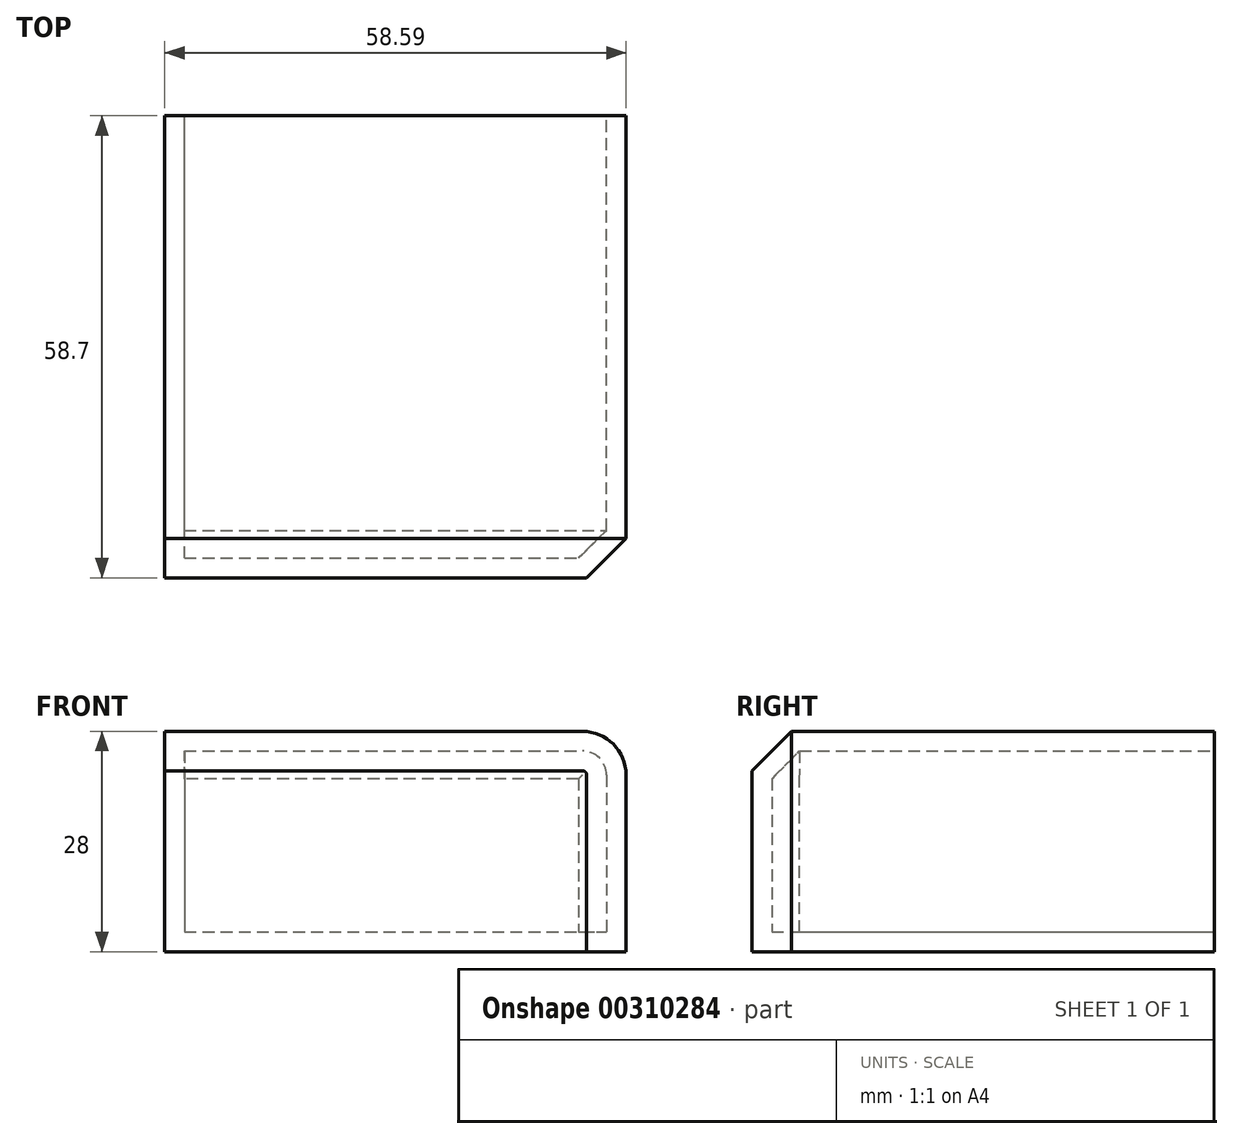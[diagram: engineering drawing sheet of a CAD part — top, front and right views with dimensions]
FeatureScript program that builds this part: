
annotation { "Feature Type Name" : "Feature", "Feature Type Description" : "" }
export const myFeature = defineFeature(function(context is Context, id is Id, definition is map)
    precondition{}
    {
        {
            var Q0;
            Q0=qCreatedBy(makeId("Top.planeOp"),FACE);
            var sketch = newSketch(context, id + "F0", { "sketchPlane" : qUnion([Q0])});
            skLineSegment(sketch, "E0.bottom", {"start": v(0, 0) * mm, "end": v(58.59, 0) * mm});
            skLineSegment(sketch, "E0.top", {"start": v(0, 58.7) * mm, "end": v(58.59, 58.7) * mm});
            skLineSegment(sketch, "E0.left", {"start": v(0, 0) * mm, "end": v(0, 58.7) * mm});
            skLineSegment(sketch, "E0.right", {"start": v(58.59, 0) * mm, "end": v(58.59, 58.7) * mm});
            skSolve(sketch);
        }
        {
            var Q0;
            Q0 = qSketchRegion(id + "F0", true);
            extrude(context, id + "F1", {"entities" : qUnion([Q0]), "depth" : 28 * mm});
        }
        {
            var Q0;
            Q0=makeQuery(id+"F1.opExtrude","CAP_EDGE",EDGE,{"disambiguationData":[OSD([sQuery(id+"F0.wireOp",EDGE,"E0.right")])],"isStart":false});
            fillet(context, id + "F2", {"entities" : qUnion([Q0]), "radius" : 5.55 * mm, "tangentPropagation" : true, "allowEdgeOverflow" : false});
        }
        {
            var Q0;
            Q0=makeQuery(id+"F1.opExtrude","CAP_EDGE",EDGE,{"disambiguationData":[OSD([sQuery(id+"F0.wireOp",EDGE,"E0.bottom")])],"isStart":false});
            chamfer(context, id + "F3", {"entities" : qUnion([Q0]), "width" : 5 * mm, "tangentPropagation" : true});
        }
        {
            var Q0;
            Q0=makeQuery(id+"F1.opExtrude","SWEPT_FACE",FACE,{"disambiguationData":[OSD([sQuery(id+"F0.wireOp",EDGE,"E0.top")])]});
            shell(context, id + "F4", {"entities" : qUnion([Q0]), "thickness" : 2.5 * mm});
        }
    });
